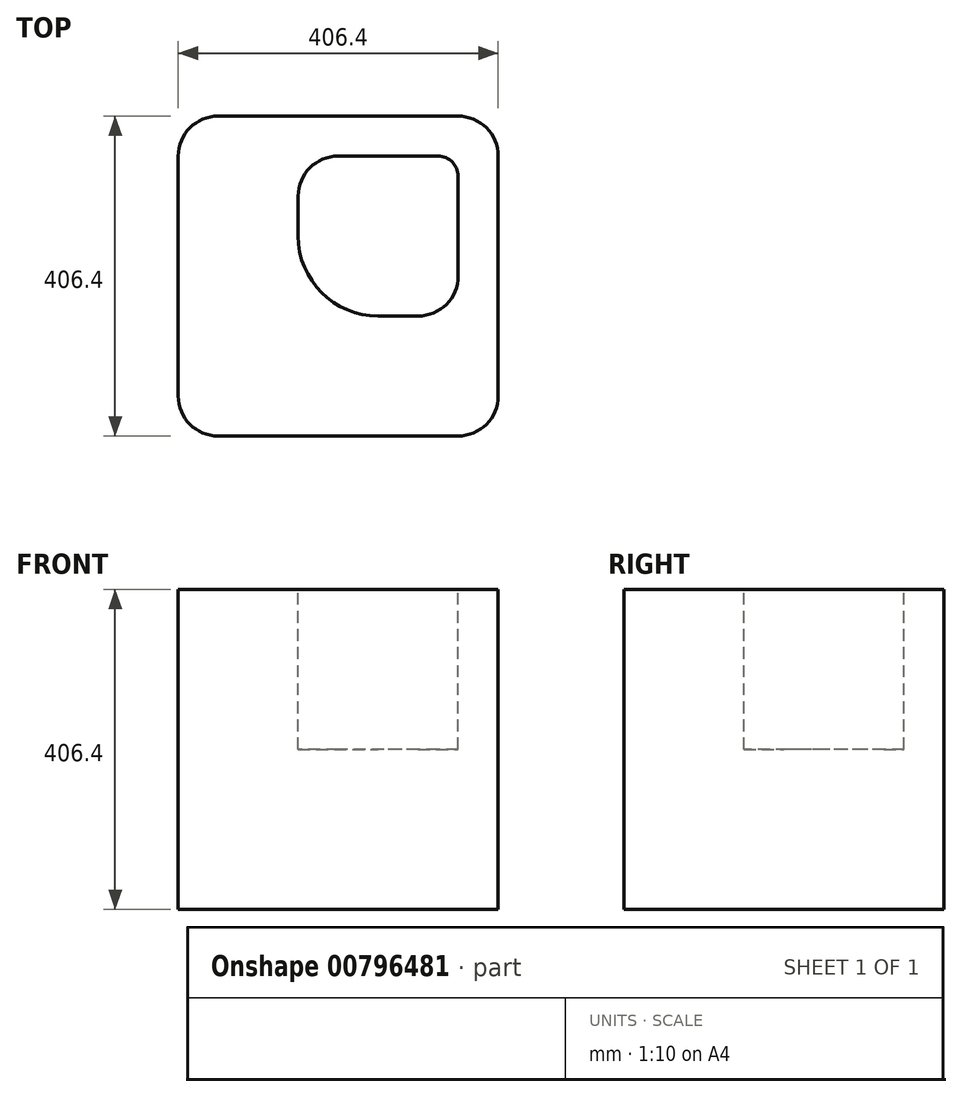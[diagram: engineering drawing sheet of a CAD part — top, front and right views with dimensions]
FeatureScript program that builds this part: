
annotation { "Feature Type Name" : "Feature", "Feature Type Description" : "" }
export const myFeature = defineFeature(function(context is Context, id is Id, definition is map)
    precondition{}
    {
        {
            var Q0;
            Q0=qCreatedBy(makeId("Top.planeOp"),FACE);
            var sketch = newSketch(context, id + "F0", { "sketchPlane" : qUnion([Q0])});
            skLineSegment(sketch, "E0.bottom", {"start": v(62.58, 0) * mm, "end": v(367.38, 0) * mm});
            skLineSegment(sketch, "E0.top", {"start": v(62.58, 406.4) * mm, "end": v(367.38, 406.4) * mm});
            skLineSegment(sketch, "E0.left", {"start": v(11.78, 50.8) * mm, "end": v(11.78, 355.6) * mm});
            skLineSegment(sketch, "E0.right", {"start": v(418.18, 50.8) * mm, "end": v(418.18, 355.6) * mm});
            skPoint(sketch, "E1.visualSharp", {"position": v(11.78, 406.4) * mm});
            skArc(sketch, "E1.filletArc", {"start": v(62.58, 406.4) * mm, "mid": v(26.66, 391.52) * mm, "end": v(11.78, 355.6) * mm});
            skPoint(sketch, "E2.visualSharp", {"position": v(418.18, 406.4) * mm});
            skArc(sketch, "E2.filletArc", {"start": v(418.18, 355.6) * mm, "mid": v(403.3, 391.52) * mm, "end": v(367.38, 406.4) * mm});
            skPoint(sketch, "E3.visualSharp", {"position": v(418.18, 0) * mm});
            skArc(sketch, "E3.filletArc", {"start": v(367.38, 0) * mm, "mid": v(403.3, 14.88) * mm, "end": v(418.18, 50.8) * mm});
            skPoint(sketch, "E4.visualSharp", {"position": v(11.78, 0) * mm});
            skArc(sketch, "E4.filletArc", {"start": v(11.78, 50.8) * mm, "mid": v(26.66, 14.88) * mm, "end": v(62.58, 0) * mm});
            skSolve(sketch);
        }
        {
            var Q0;
            Q0 = qSketchRegion(id + "F0", true);
            extrude(context, id + "F1", {"entities" : qUnion([Q0]), "depth" : 406.4 * mm, "offsetDistance" : 25.4 * mm});
        }
        {
            var Q0;
            Q0=makeQuery(id+"F1.opExtrude","CAP_FACE",FACE,{"disambiguationData":[OSD([sQuery(id+"F0.wireOp",EDGE,"E0.bottom"),sQuery(id+"F0.wireOp",EDGE,"E0.top"),sQuery(id+"F0.wireOp",EDGE,"E0.left"),sQuery(id+"F0.wireOp",EDGE,"E0.right"),sQuery(id+"F0.wireOp",EDGE,"E1.filletArc"),sQuery(id+"F0.wireOp",EDGE,"E2.filletArc"),sQuery(id+"F0.wireOp",EDGE,"E3.filletArc"),sQuery(id+"F0.wireOp",EDGE,"E4.filletArc")])],"isStart":false});
            var sketch = newSketch(context, id + "F2", { "sketchPlane" : qUnion([Q0])});
            skLineSegment(sketch, "E5.bottom", {"start": v(341.98, 355.6) * mm, "end": v(214.98, 355.6) * mm});
            skLineSegment(sketch, "E5.top", {"start": v(316.58, 152.4) * mm, "end": v(265.78, 152.4) * mm});
            skLineSegment(sketch, "E5.left", {"start": v(367.38, 330.2) * mm, "end": v(367.38, 203.2) * mm});
            skLineSegment(sketch, "E5.right", {"start": v(164.18, 304.8) * mm, "end": v(164.18, 254) * mm});
            skPoint(sketch, "E6.visualSharp", {"position": v(164.18, 152.4) * mm});
            skArc(sketch, "E6.filletArc", {"start": v(164.18, 254) * mm, "mid": v(193.94, 182.16) * mm, "end": v(265.78, 152.4) * mm});
            skPoint(sketch, "E7.visualSharp", {"position": v(367.38, 152.4) * mm});
            skArc(sketch, "E7.filletArc", {"start": v(316.58, 152.4) * mm, "mid": v(352.5, 167.28) * mm, "end": v(367.38, 203.2) * mm});
            skPoint(sketch, "E8.visualSharp", {"position": v(164.18, 355.6) * mm});
            skArc(sketch, "E8.filletArc", {"start": v(214.98, 355.6) * mm, "mid": v(179.06, 340.72) * mm, "end": v(164.18, 304.8) * mm});
            skPoint(sketch, "E9.visualSharp", {"position": v(367.38, 355.6) * mm});
            skArc(sketch, "E9.filletArc", {"start": v(367.38, 330.2) * mm, "mid": v(359.94, 348.16) * mm, "end": v(341.98, 355.6) * mm});
            skSolve(sketch);
        }
        {
            var Q0;
            Q0 = qSketchRegion(id + "F2", true);
            extrude(context, id + "F3", {"entities" : qUnion([Q0]), "operationType" : NewBodyOperationType.REMOVE, "oppositeDirection" : true, "depth" : 203.2 * mm, "offsetDistance" : 25.4 * mm});
        }
    });
